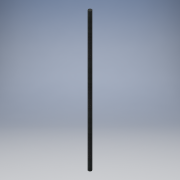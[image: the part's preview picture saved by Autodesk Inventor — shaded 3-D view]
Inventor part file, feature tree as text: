
AUTODESK INVENTOR PART (.ipt)
format: ipt  version: 2016 (Build 200138000, 138)  size: 96,256 bytes
history: native  units: in
note: dims shown in document units (in); Inventor stores cm internally (conversion verified against a paired STEP export)
features: extrude x1, sketch x1
ambient origin geometry x8: Origin, YZ Plane, XZ Plane, XY Plane, X Axis, Y Axis, Z Axis, Center Point
bodies: Solid1 (feature_tree)
feature tree (2):
  extrude  "Extrusion1"  Depth=22.0in TaperAngle=0.0deg
  sketch  "Sketch1"  dims[d0=0.5in d1=22.0in d2=0.0in]
